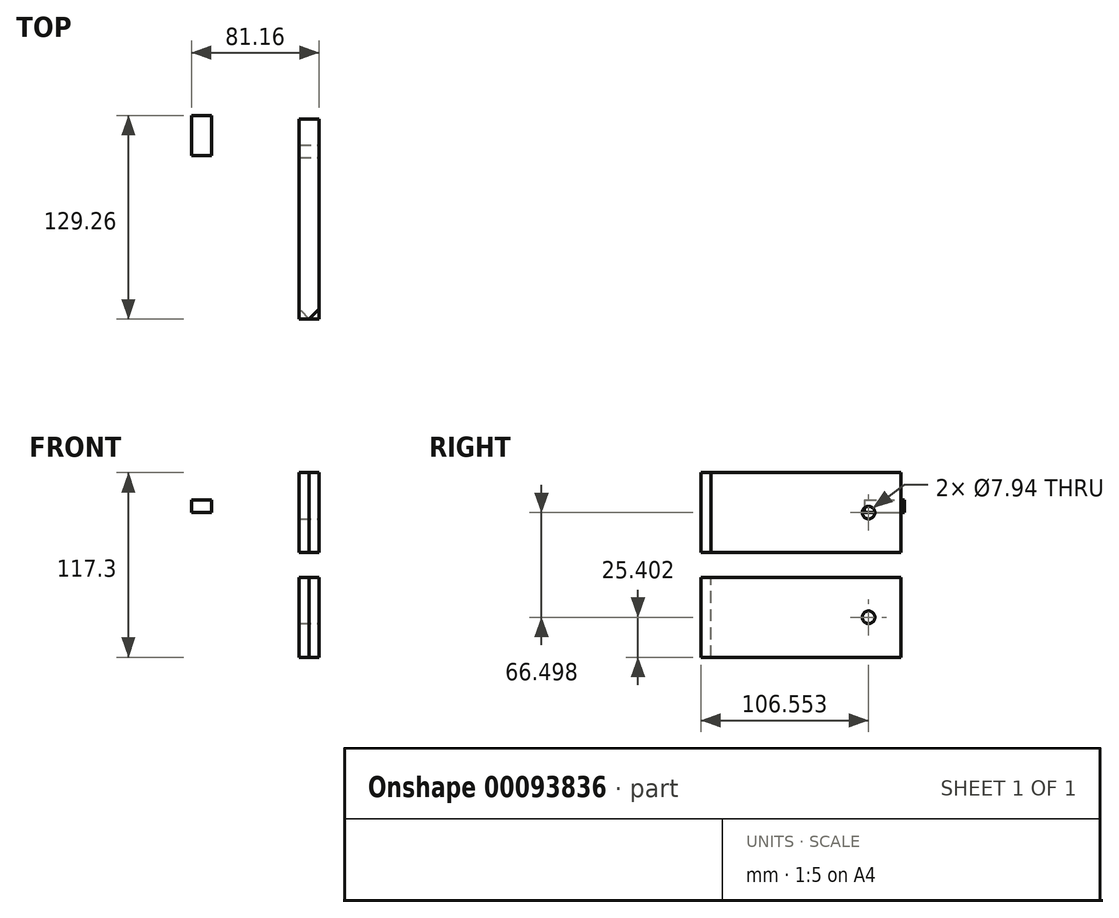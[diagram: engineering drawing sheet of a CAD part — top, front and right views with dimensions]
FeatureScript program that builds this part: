
annotation { "Feature Type Name" : "Feature", "Feature Type Description" : "" }
export const myFeature = defineFeature(function(context is Context, id is Id, definition is map)
    precondition{}
    {
        {
            var Q0;
            Q0=qCreatedBy(makeId("Right.planeOp"),FACE);
            var sketch = newSketch(context, id + "F0", { "sketchPlane" : qUnion([Q0])});
            skLineSegment(sketch, "E0.bottom", {"start": v(63.5, 25.4) * mm, "end": v(-63.5, 25.4) * mm});
            skLineSegment(sketch, "E0.top", {"start": v(63.5, -25.4) * mm, "end": v(-63.5, -25.4) * mm});
            skLineSegment(sketch, "E0.left", {"start": v(63.5, 25.4) * mm, "end": v(63.5, -25.4) * mm});
            skLineSegment(sketch, "E0.right", {"start": v(-63.5, 25.4) * mm, "end": v(-63.5, -25.4) * mm});
            skPoint(sketch, "E0.middle", {"position": v(0, 0) * mm});
            skSolve(sketch);
        }
        {
            var Q0;
            Q0 = qSketchRegion(id + "F0", true);
            extrude(context, id + "F1", {"entities" : qUnion([Q0]), "depth" : 12.7 * mm});
        }
        {
            var Q0;
            Q0=makeQuery(id+"F1.opExtrude","CAP_EDGE",EDGE,{"disambiguationData":[OSD([sQuery(id+"F0.wireOp",EDGE,"E0.right")])],"isStart":false});
            chamfer(context, id + "F2", {"entities" : qUnion([Q0]), "width" : 6.35 * mm, "tangentPropagation" : true});
        }
        {
            var Q0;
            Q0=qCreatedBy(makeId("Right.planeOp"),FACE);
            var sketch = newSketch(context, id + "F3", { "sketchPlane" : qUnion([Q0])});
            skLineSegment(sketch, "E1.bottom", {"start": v(63.5, -41.1) * mm, "end": v(-63.5, -41.1) * mm});
            skLineSegment(sketch, "E1.top", {"start": v(63.5, -91.9) * mm, "end": v(-63.5, -91.9) * mm});
            skLineSegment(sketch, "E1.left", {"start": v(63.5, -41.1) * mm, "end": v(63.5, -91.9) * mm});
            skLineSegment(sketch, "E1.right", {"start": v(-63.5, -41.1) * mm, "end": v(-63.5, -91.9) * mm});
            skPoint(sketch, "E1.middle", {"position": v(0, -66.5) * mm});
            skSolve(sketch);
        }
        {
            var Q0;
            Q0 = qSketchRegion(id + "F3", true);
            extrude(context, id + "F4", {"entities" : qUnion([Q0]), "depth" : 12.7 * mm});
        }
        {
            var Q0;
            Q0=makeQuery(id+"F4.opExtrude","CAP_EDGE",EDGE,{"disambiguationData":[OSD([sQuery(id+"F3.wireOp",EDGE,"E1.right")])],"isStart":true});
            chamfer(context, id + "F5", {"entities" : qUnion([Q0]), "width" : 6.35 * mm, "tangentPropagation" : true});
        }
        {
            var Q0;
            Q0=makeQuery(id+"F1.opExtrude","CAP_FACE",FACE,{"disambiguationData":[OSD([sQuery(id+"F0.wireOp",EDGE,"E0.bottom"),sQuery(id+"F0.wireOp",EDGE,"E0.top"),sQuery(id+"F0.wireOp",EDGE,"E0.left"),sQuery(id+"F0.wireOp",EDGE,"E0.right")])],"isStart":false});
            var sketch = newSketch(context, id + "F6", { "sketchPlane" : qUnion([Q0])});
            skLineSegment(sketch, "E2", {"start": v(63.5, 0) * mm, "end": v(43.05, 0) * mm});
            skCircle(sketch, "E3", {"center": v(43.05, 0) * mm, "radius": 3.97 * mm});
            skSolve(sketch);
        }
        {
            var Q0;
            Q0 = qSketchRegion(id + "F6", true);
            extrude(context, id + "F7", {"entities" : qUnion([Q0]), "operationType" : NewBodyOperationType.REMOVE, "endBound" : BoundingType.THROUGH_ALL, "oppositeDirection" : true, "depth" : 25.4 * mm});
        }
        {
            var Q0;
            Q0=makeQuery(id+"F4.opExtrude","CAP_FACE",FACE,{"disambiguationData":[OSD([sQuery(id+"F3.wireOp",EDGE,"E1.bottom"),sQuery(id+"F3.wireOp",EDGE,"E1.top"),sQuery(id+"F3.wireOp",EDGE,"E1.left"),sQuery(id+"F3.wireOp",EDGE,"E1.right")])],"isStart":false});
            var sketch = newSketch(context, id + "F8", { "sketchPlane" : qUnion([Q0])});
            skLineSegment(sketch, "E4", {"start": v(63.5, -66.5) * mm, "end": v(43.05, -66.5) * mm});
            skCircle(sketch, "E5", {"center": v(43.05, -66.5) * mm, "radius": 3.97 * mm});
            skSolve(sketch);
        }
        {
            var Q0;
            Q0 = qSketchRegion(id + "F8", true);
            extrude(context, id + "F9", {"entities" : qUnion([Q0]), "operationType" : NewBodyOperationType.REMOVE, "endBound" : BoundingType.THROUGH_ALL, "oppositeDirection" : true, "depth" : 25.4 * mm});
        }
        {
            var Q0;
            Q0=qCreatedBy(makeId("Top.planeOp"),FACE);
            var sketch = newSketch(context, id + "F10", { "sketchPlane" : qUnion([Q0])});
            skLineSegment(sketch, "E6.bottom", {"start": v(-55.76, 40.36) * mm, "end": v(-68.46, 40.36) * mm});
            skLineSegment(sketch, "E6.top", {"start": v(-55.76, 65.76) * mm, "end": v(-68.46, 65.76) * mm});
            skLineSegment(sketch, "E6.left", {"start": v(-55.76, 40.36) * mm, "end": v(-55.76, 65.76) * mm});
            skLineSegment(sketch, "E6.right", {"start": v(-68.46, 40.36) * mm, "end": v(-68.46, 65.76) * mm});
            skPoint(sketch, "E6.middle", {"position": v(-62.1, 53.06) * mm});
            skSolve(sketch);
        }
        {
            var Q0;
            Q0 = qSketchRegion(id + "F10", true);
            extrude(context, id + "F11", {"entities" : qUnion([Q0]), "depth" : 7.94 * mm});
        }
    });
